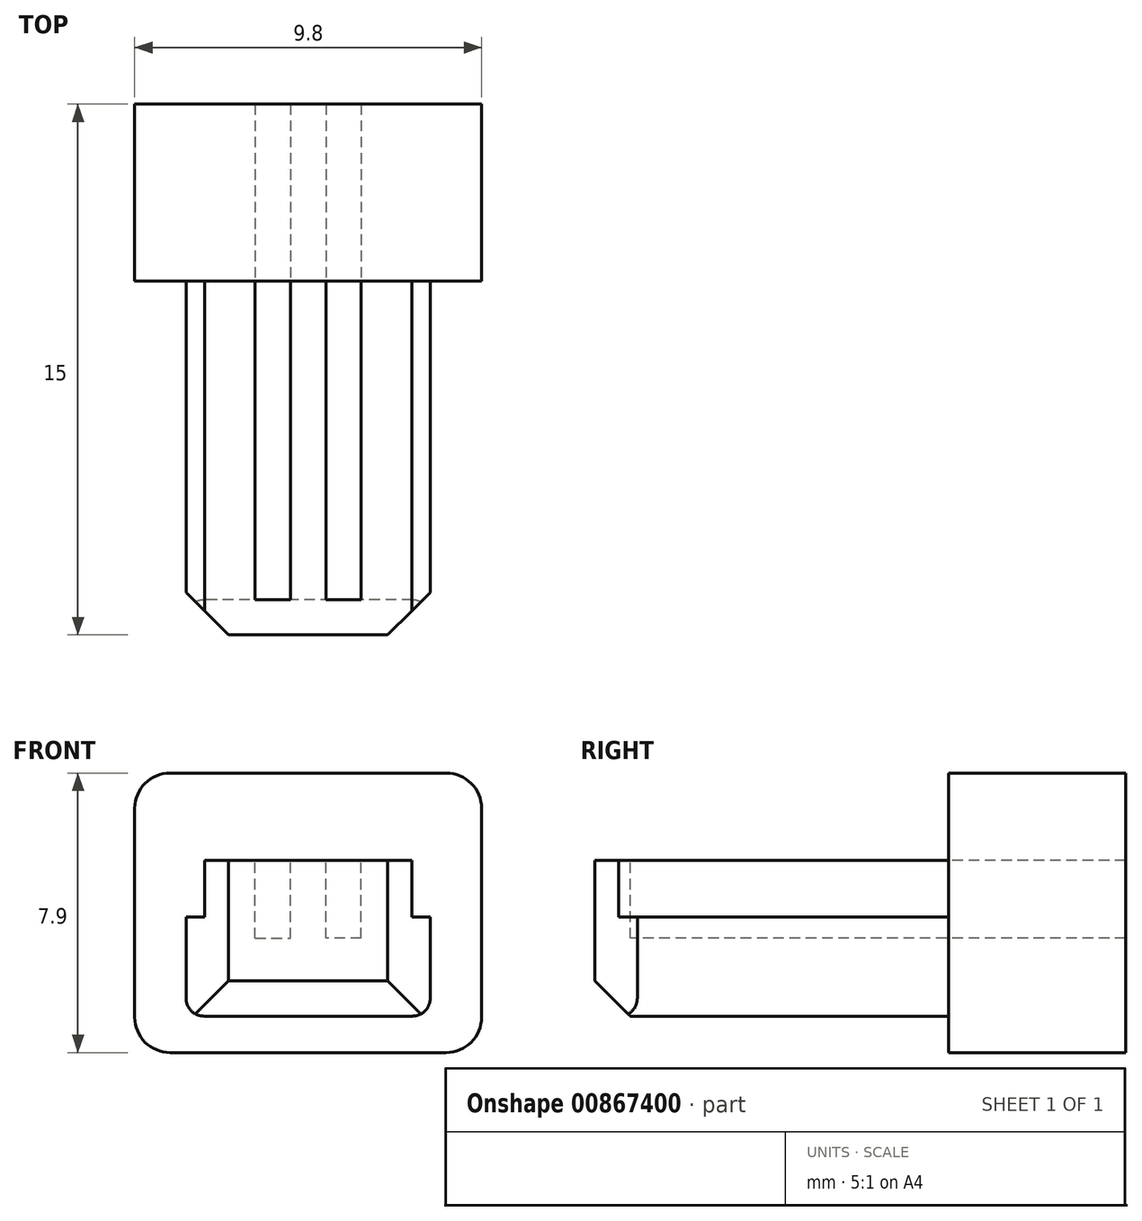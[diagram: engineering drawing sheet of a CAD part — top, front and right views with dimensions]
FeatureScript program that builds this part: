
annotation { "Feature Type Name" : "Feature", "Feature Type Description" : "" }
export const myFeature = defineFeature(function(context is Context, id is Id, definition is map)
    precondition{}
    {
        {
            var Q0;
            Q0=qCreatedBy(makeId("Front.planeOp"),FACE);
            var sketch = newSketch(context, id + "F0", { "sketchPlane" : qUnion([Q0])});
            skLineSegment(sketch, "E0.bottom", {"start": v(-3.45, 0) * mm, "end": v(3.45, 0) * mm});
            skLineSegment(sketch, "E0.left", {"start": v(-3.45, 0) * mm, "end": v(-3.45, 2.8) * mm});
            skLineSegment(sketch, "E0.right", {"start": v(3.45, 0) * mm, "end": v(3.45, 2.8) * mm});
            skLineSegment(sketch, "E1", {"start": v(-3.45, 2.8) * mm, "end": v(-2.92, 2.8) * mm});
            skLineSegment(sketch, "E2", {"start": v(-2.92, 4.4) * mm, "end": v(2.92, 4.4) * mm});
            skPoint(sketch, "E3", {"position": v(0, 2.8) * mm});
            skPoint(sketch, "E4", {"position": v(0, 4.4) * mm});
            skLineSegment(sketch, "E5", {"start": v(-2.92, 4.4) * mm, "end": v(-2.92, 2.8) * mm});
            skLineSegment(sketch, "E6", {"start": v(2.92, 4.4) * mm, "end": v(2.92, 2.8) * mm});
            skLineSegment(sketch, "E7.trimOffspring", {"start": v(2.93, 2.8) * mm, "end": v(3.45, 2.8) * mm});
            skSolve(sketch);
        }
        {
            var Q0;
            Q0 = qSketchRegion(id + "F0", true);
            extrude(context, id + "F1", {"entities" : qUnion([Q0]), "depth" : 10 * mm, "offsetDistance" : 25 * mm});
        }
        {
            var Q0;
            Q0=makeQuery(id+"F1.opExtrude","CAP_EDGE",EDGE,{"disambiguationData":[OSD([sQuery(id+"F0.wireOp",EDGE,"E0.right")])],"isStart":false});
            var Q1;
            Q1=makeQuery(id+"F1.opExtrude","CAP_EDGE",EDGE,{"disambiguationData":[OSD([sQuery(id+"F0.wireOp",EDGE,"E0.left")])],"isStart":false});
            chamfer(context, id + "F2", {"entities" : qUnion([Q0, Q1]), "width" : 1.2 * mm, "tangentPropagation" : true});
        }
        {
            var Q0;
            Q0=makeQuery(id+"F1.opExtrude","SWEPT_EDGE",EDGE,{"disambiguationData":[OSD([sQuery(id+"F0.wireOp",EDGE,"E0.bottom"),sQuery(id+"F0.wireOp",EDGE,"E0.left")])]});
            var Q1;
            Q1=makeQuery(id+"F1.opExtrude","SWEPT_EDGE",EDGE,{"disambiguationData":[OSD([sQuery(id+"F0.wireOp",EDGE,"E0.bottom"),sQuery(id+"F0.wireOp",EDGE,"E0.right")])]});
            fillet(context, id + "F3", {"entities" : qUnion([Q0, Q1]), "radius" : .5 * mm, "tangentPropagation" : true, "allowEdgeOverflow" : false});
        }
        {
            var Q0;
            Q0=qCreatedBy(makeId("Top.planeOp"),FACE);
            cPlane(context, id + "F4", {"entities" : qUnion([Q0]), "cplaneType" : CPlaneType.OFFSET, "offset" : 4.4 * mm, "width" : 150 * mm, "height" : 150 * mm});
        }
        {
            var Q0;
            Q0=qCreatedBy(makeId("Front.planeOp"),FACE);
            var sketch = newSketch(context, id + "F5", { "sketchPlane" : qUnion([Q0])});
            skLineSegment(sketch, "E8.bottom", {"start": v(4.9, 6.87) * mm, "end": v(-4.9, 6.87) * mm});
            skLineSegment(sketch, "E8.top", {"start": v(4.9, -1.03) * mm, "end": v(-4.9, -1.03) * mm});
            skLineSegment(sketch, "E8.left", {"start": v(4.9, 6.87) * mm, "end": v(4.9, -1.03) * mm});
            skLineSegment(sketch, "E8.right", {"start": v(-4.9, 6.87) * mm, "end": v(-4.9, -1.03) * mm});
            skPoint(sketch, "E9", {"position": v(0, 6.87) * mm});
            skSolve(sketch);
        }
        {
            var Q0;
            Q0 = qSketchRegion(id + "F5", true);
            extrude(context, id + "F6", {"entities" : qUnion([Q0]), "operationType" : NewBodyOperationType.ADD, "oppositeDirection" : true, "depth" : 5 * mm, "offsetDistance" : 25 * mm});
        }
        {
            var Q0;
            Q0=qCreatedBy(id+"F4.planeOp",FACE);
            var sketch = newSketch(context, id + "F7", { "sketchPlane" : qUnion([Q0])});
            skLineSegment(sketch, "E10.top", {"start": v(-1.5, -9) * mm, "end": v(-0.5, -9) * mm});
            skLineSegment(sketch, "E10.left", {"start": v(-1.5, 0) * mm, "end": v(-1.5, -9) * mm});
            skLineSegment(sketch, "E10.right", {"start": v(-0.5, 5) * mm, "end": v(-0.5, -9) * mm});
            skLineSegment(sketch, "E11.MirrorCS", {"start": v(0.5, 5) * mm, "end": v(0.5, -9) * mm});
            skLineSegment(sketch, "E12.MirrorCS", {"start": v(1.5, 0) * mm, "end": v(1.5, -9) * mm});
            skLineSegment(sketch, "E13.MirrorCS", {"start": v(1.5, -9) * mm, "end": v(0.5, -9) * mm});
            skLineSegment(sketch, "E14", {"start": v(-1.5, 0) * mm, "end": v(-1.5, 5) * mm});
            skLineSegment(sketch, "E15", {"start": v(1.5, 0) * mm, "end": v(1.5, 5) * mm});
            skLineSegment(sketch, "E16", {"start": v(1.5, 5) * mm, "end": v(0.5, 5) * mm});
            skLineSegment(sketch, "E17", {"start": v(-1.5, 5) * mm, "end": v(-0.5, 5) * mm});
            skSolve(sketch);
        }
        {
            var Q0;
            Q0 = qSketchRegion(id + "F7", true);
            extrude(context, id + "F8", {"entities" : qUnion([Q0]), "operationType" : NewBodyOperationType.REMOVE, "oppositeDirection" : true, "depth" : 2.2 * mm, "offsetDistance" : 25 * mm});
        }
        {
            var Q0;
            Q0=makeQuery(id+"F1.opExtrude","CAP_EDGE",EDGE,{"disambiguationData":[OSD([sQuery(id+"F0.wireOp",EDGE,"E0.bottom")])],"isStart":false});
            chamfer(context, id + "F9", {"entities" : qUnion([Q0]), "width" : 1 * mm, "tangentPropagation" : true});
        }
        {
            var Q0;
            Q0=makeQuery(id+"F6.opExtrude","SWEPT_EDGE",EDGE,{"disambiguationData":[OSD([sQuery(id+"F5.wireOp",EDGE,"E8.bottom"),sQuery(id+"F5.wireOp",EDGE,"E8.left")])]});
            var Q1;
            Q1=makeQuery(id+"F6.opExtrude","SWEPT_EDGE",EDGE,{"disambiguationData":[OSD([sQuery(id+"F5.wireOp",EDGE,"E8.top"),sQuery(id+"F5.wireOp",EDGE,"E8.left")])]});
            var Q2;
            Q2=makeQuery(id+"F6.opExtrude","SWEPT_EDGE",EDGE,{"disambiguationData":[OSD([sQuery(id+"F5.wireOp",EDGE,"E8.top"),sQuery(id+"F5.wireOp",EDGE,"E8.right")])]});
            var Q3;
            Q3=makeQuery(id+"F6.opExtrude","SWEPT_EDGE",EDGE,{"disambiguationData":[OSD([sQuery(id+"F5.wireOp",EDGE,"E8.bottom"),sQuery(id+"F5.wireOp",EDGE,"E8.right")])]});
            fillet(context, id + "F10", {"entities" : qUnion([Q0, Q1, Q2, Q3]), "radius" : 1 * mm, "tangentPropagation" : true, "allowEdgeOverflow" : false});
        }
    });
